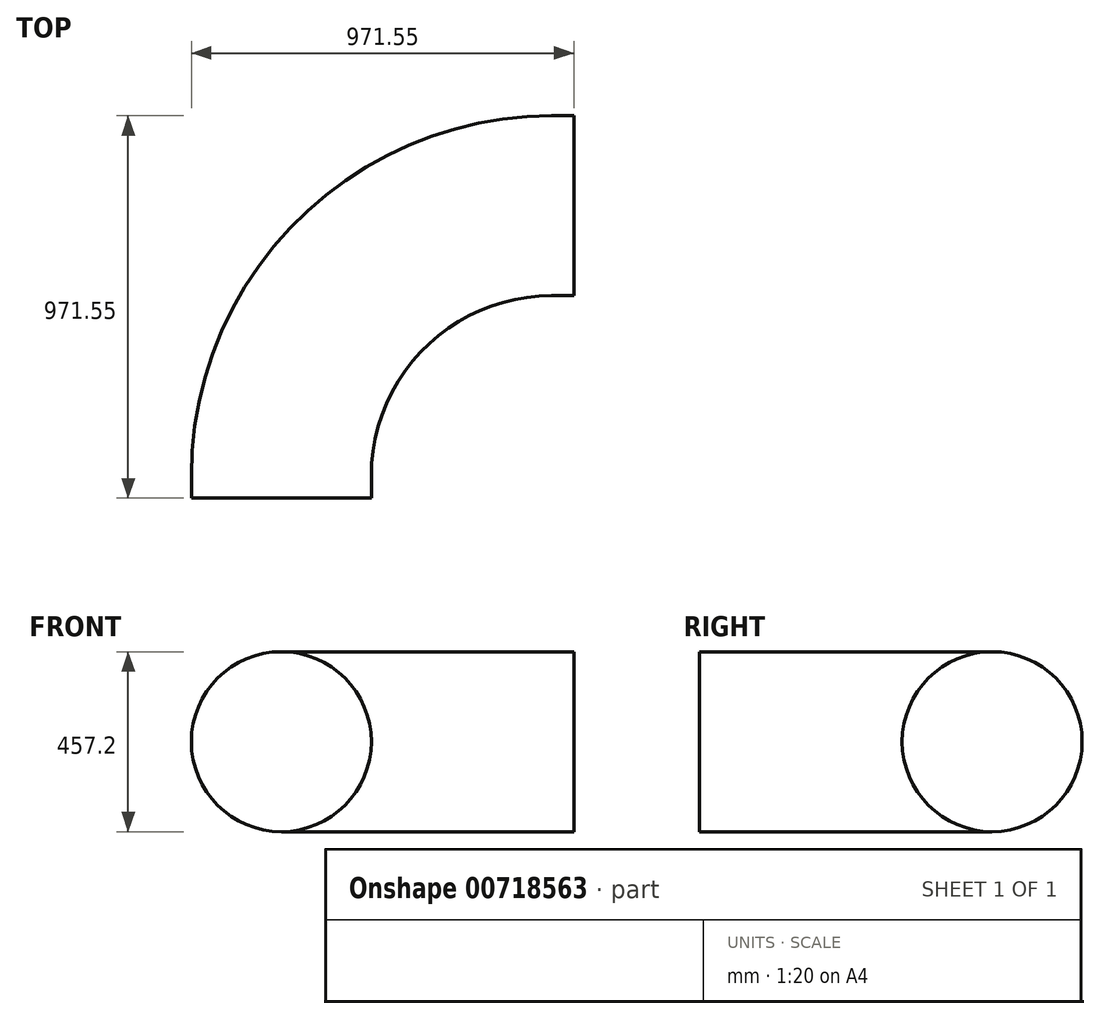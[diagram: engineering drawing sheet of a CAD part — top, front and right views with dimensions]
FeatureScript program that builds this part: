
annotation { "Feature Type Name" : "Feature", "Feature Type Description" : "" }
export const myFeature = defineFeature(function(context is Context, id is Id, definition is map)
    precondition{}
    {
        {
            var Q0;
            Q0=qCreatedBy(makeId("Front.planeOp"),FACE);
            var sketch = newSketch(context, id + "F0", { "sketchPlane" : qUnion([Q0])});
            skLineSegment(sketch, "E0", {"start": v(0, 0) * mm, "end": v(-685.8, 0) * mm, "construction": true});
            skCircle(sketch, "E1", {"center": v(-685.8, 0) * mm, "radius": 228.6 * mm});
            skSolve(sketch);
        }
        {
            var Q0;
            Q0=qCreatedBy(makeId("Top.planeOp"),FACE);
            var sketch = newSketch(context, id + "F1", { "sketchPlane" : qUnion([Q0])});
            skArc(sketch, "E2", {"start": v(0, 457.2) * mm, "mid": v(-323.29, 323.29) * mm, "end": v(-457.2, 0) * mm});
            skLineSegment(sketch, "E3", {"start": v(0, 0) * mm, "end": v(-505.33, 0) * mm, "construction": true});
            skLineSegment(sketch, "E4", {"start": v(0, 0) * mm, "end": v(0, 518.45) * mm, "construction": true});
            skSolve(sketch);
        }
        {
            var Q0;
            Q0=makeQuery(id+"F0.imprint","IMPRINT",FACE,{"disambiguationData":[TD([[makeQuery(id+"F0.imprint","IMPRINT",EDGE,{"derivedFrom":sQuery(id+"F0.wireOp",EDGE,"E1")}),1.0]])]});
            var Q1;
            Q1 = qConstructionFilter(qBodyType(qCreatedBy(id + "F1" ,EDGE), BodyType.WIRE), ConstructionObject.NO);
            sweep(context, id + "F2", {"profiles" : qUnion([Q0]), "path" : qUnion([Q1])});
        }
        {
            var Q0;
            Q0=makeQuery(id+"F2.opSweep","CAP_FACE",FACE,{"disambiguationData":[OSD([sQuery(id+"F0.wireOp",EDGE,"E1"),sQuery(id+"F1.wireOp",VERTEX,"E2.end")])],"isStart":true});
            extrude(context, id + "F3", {"entities" : qUnion([Q0]), "operationType" : NewBodyOperationType.ADD, "depth" : 57.15 * mm, "offsetDistance" : 25.4 * mm});
        }
        {
            var Q0;
            Q0=makeQuery(id+"F2.opSweep","CAP_FACE",FACE,{"disambiguationData":[OSD([sQuery(id+"F0.wireOp",EDGE,"E1"),sQuery(id+"F1.wireOp",VERTEX,"E2.start")])],"isStart":false});
            extrude(context, id + "F4", {"entities" : qUnion([Q0]), "operationType" : NewBodyOperationType.ADD, "depth" : 57.15 * mm, "offsetDistance" : 25.4 * mm});
        }
    });
